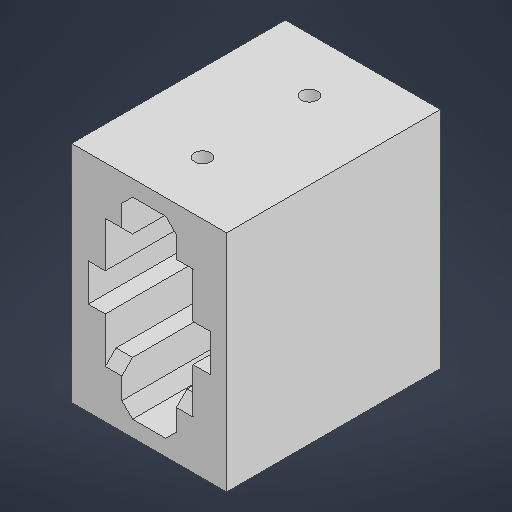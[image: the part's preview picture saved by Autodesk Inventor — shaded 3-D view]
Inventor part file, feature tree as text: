
AUTODESK INVENTOR PART (.ipt)
format: ipt  version: 2025.1 (Build 291241000, 241)  size: 566,784 bytes
history: native  units: mm
features: extrude x7, sketch x5, projected_geometry x4, mirror x3, chamfer x2, plane x1
ambient origin geometry x8: Origin, YZ Plane, XZ Plane, XY Plane, X Axis, Y Axis, Z Axis, Center Point
bodies: Solid1 (feature_tree)
feature tree (22):
  sketch  "Sketch1"  dims[d2=5.0mm d4=42.0mm d5=0.0mm]
  extrude  "Extrusion1"  Depth=42.0mm TaperAngle=0.0deg
  extrude  "Extrusion2"  TaperAngle=0.0deg  [1 undecoded]
  extrude  "Extrusion3"  Depth=3.2mm
  extrude  "Extrusion4"  Depth=11.0mm TaperAngle=0.0deg
  extrude  "Extrusion5"  Depth=3.0mm TaperAngle=0.0deg
  chamfer  "Chamfer1"  Distance=2.0mm Angle=45.0deg
  chamfer  "Chamfer2"  Distance=2.0mm Angle=45.0deg
  plane  "Work Plane1"
  mirror  "Mirror1"
  extrude  "Extrusion6"  Depth=29.0mm
  extrude  "Extrusion7"  Depth=10.2mm
  mirror  "Mirror2"
  mirror  "Mirror3"
  sketch  "Sketch2"  dims[d6=7.0mm d8=0.0mm]
  projected_geometry  "Projected Loop1"
  sketch  "Sketch3"  dims[d9=3.2mm d10=0.0mm d11=3.8mm]
  projected_geometry  "Projected Loop2"
  sketch  "Sketch4"  dims[d12=10.0mm d13=0.0mm d14=11.0mm d15=0.0mm]
  projected_geometry  "Projected Loop3"
  sketch  "Sketch5"  dims[d17=5.0mm d18=3.0mm d19=0.0mm d20=2.0mm d21=2.0mm d22=45.0deg d23=2.0mm d24=2.0mm d25=45.0deg d26=29.0mm d27=10.2mm d28=16.4mm d29=40.0mm d30=3.0mm d31=10.0mm d32=20.0mm d33=10.0mm d34=0.0mm d35=8.0mm d36=3.0mm d37=6.0mm d38=0.0mm d39=15.0mm d40=30.0mm]
  projected_geometry  "Projected Loop4"
note: 1 required parameter value undecoded (feature->parameter linkage not recoverable at this tier; creation-order binding heuristic only, values carry confidence <= 0.55)
